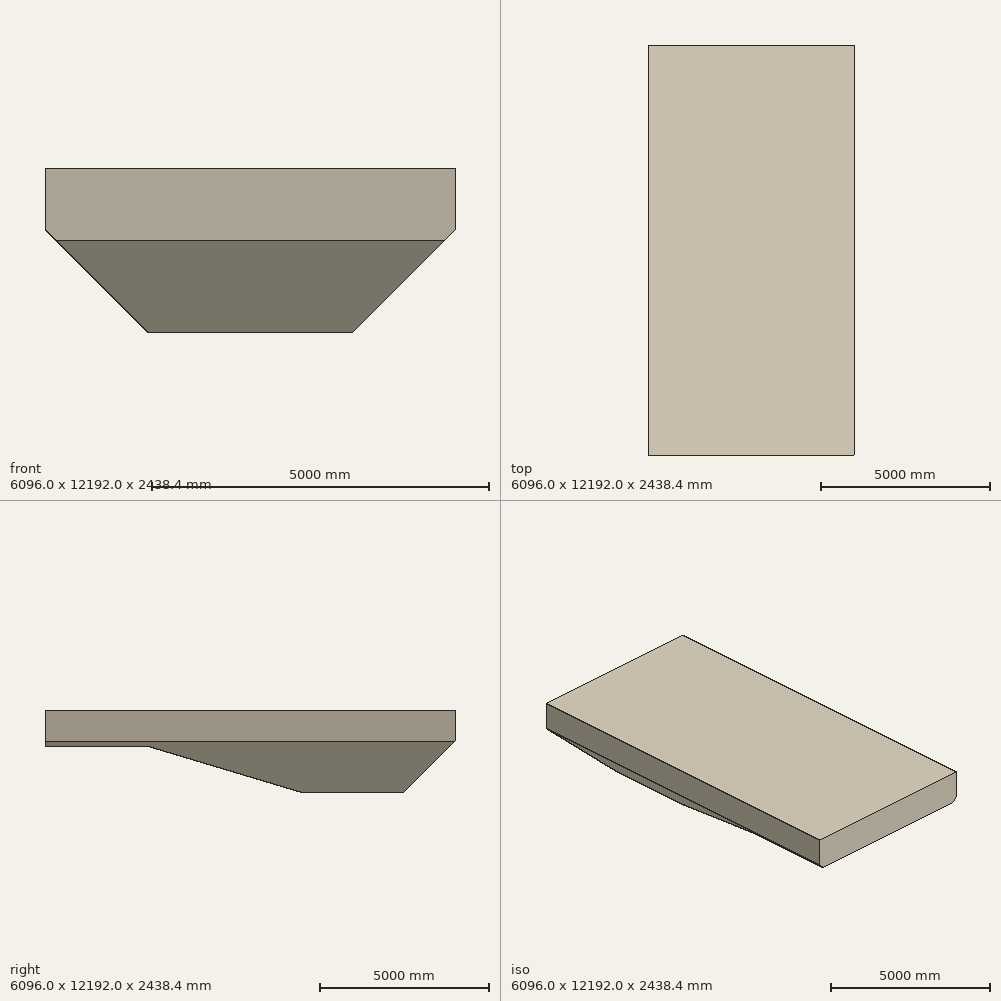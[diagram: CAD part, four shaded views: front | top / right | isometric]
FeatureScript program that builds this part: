
annotation { "Feature Type Name" : "Feature", "Feature Type Description" : "" }
export const myFeature = defineFeature(function(context is Context, id is Id, definition is map)
    precondition{}
    {
        {
            var Q0;
            Q0=qCreatedBy(makeId("Top.planeOp"),FACE);
            var sketch = newSketch(context, id + "F0", { "sketchPlane" : qUnion([Q0])});
            skLineSegment(sketch, "E0.bottom", {"start": v(0, 0) * mm, "end": v(6096, 0) * mm});
            skLineSegment(sketch, "E0.top", {"start": v(0, 12192) * mm, "end": v(6096, 12192) * mm});
            skLineSegment(sketch, "E0.left", {"start": v(0, 0) * mm, "end": v(0, 12192) * mm});
            skLineSegment(sketch, "E0.right", {"start": v(6096, 0) * mm, "end": v(6096, 12192) * mm});
            skSolve(sketch);
        }
        {
            var Q0;
            Q0 = qSketchRegion(id + "F0", true);
            extrude(context, id + "F1", {"entities" : qUnion([Q0]), "depth" : 2438.4 * mm});
        }
        {
            var Q0;
            Q0=makeQuery(id+"F1.opExtrude","SWEPT_FACE",FACE,{"disambiguationData":[OSD([sQuery(id+"F0.wireOp",EDGE,"E0.right")])]});
            var sketch = newSketch(context, id + "F2", { "sketchPlane" : qUnion([Q0])});
            skLineSegment(sketch, "E1", {"start": v(0, 0) * mm, "end": v(0, 1371.6) * mm});
            skLineSegment(sketch, "E2", {"start": v(0, 1371.6) * mm, "end": v(3048, 1371.6) * mm});
            skLineSegment(sketch, "E3", {"start": v(3048, 1371.6) * mm, "end": v(7620, 0) * mm});
            skLineSegment(sketch, "E4", {"start": v(7620, 0) * mm, "end": v(0, 0) * mm});
            skSolve(sketch);
        }
        {
            var Q0;
            Q0 = qSketchRegion(id + "F2", true);
            extrude(context, id + "F3", {"entities" : qUnion([Q0]), "operationType" : NewBodyOperationType.REMOVE, "endBound" : BoundingType.UP_TO_NEXT, "oppositeDirection" : true, "depth" : 25.4 * mm});
        }
        {
            var Q0;
            Q0=makeQuery(id+"F1.opExtrude","SWEPT_FACE",FACE,{"disambiguationData":[OSD([sQuery(id+"F0.wireOp",EDGE,"E0.right")])]});
            var sketch = newSketch(context, id + "F4", { "sketchPlane" : qUnion([Q0])});
            skLineSegment(sketch, "E5", {"start": v(12192, 0) * mm, "end": v(10668, 0) * mm});
            skLineSegment(sketch, "E6", {"start": v(10668, 0) * mm, "end": v(12192, 1524) * mm});
            skLineSegment(sketch, "E7", {"start": v(12192, 1524) * mm, "end": v(12192, 0) * mm});
            skSolve(sketch);
        }
        {
            var Q0;
            Q0 = qSketchRegion(id + "F4", true);
            extrude(context, id + "F5", {"entities" : qUnion([Q0]), "operationType" : NewBodyOperationType.REMOVE, "endBound" : BoundingType.UP_TO_NEXT, "oppositeDirection" : true, "depth" : 25.4 * mm});
        }
        {
            var Q0;
            Q0=makeQuery(id+"F1.opExtrude","SWEPT_FACE",FACE,{"disambiguationData":[OSD([sQuery(id+"F0.wireOp",EDGE,"E0.top")])]});
            var sketch = newSketch(context, id + "F6", { "sketchPlane" : qUnion([Q0])});
            skLineSegment(sketch, "E8", {"start": v(-6096, 1524) * mm, "end": v(-4572, 0) * mm});
            skLineSegment(sketch, "E9", {"start": v(-4572, 0) * mm, "end": v(-6096, 0) * mm});
            skLineSegment(sketch, "E10", {"start": v(-6096, 0) * mm, "end": v(-6096, 1524) * mm});
            skLineSegment(sketch, "E11", {"start": v(0, 1524) * mm, "end": v(0, 0) * mm});
            skLineSegment(sketch, "E12", {"start": v(0, 0) * mm, "end": v(-1524, 0) * mm});
            skLineSegment(sketch, "E13", {"start": v(-1524, 0) * mm, "end": v(0, 1524) * mm});
            skSolve(sketch);
        }
        {
            var Q0;
            Q0 = qSketchRegion(id + "F6", true);
            extrude(context, id + "F7", {"entities" : qUnion([Q0]), "operationType" : NewBodyOperationType.REMOVE, "endBound" : BoundingType.THROUGH_ALL, "oppositeDirection" : true, "depth" : 25.4 * mm});
        }
    });
